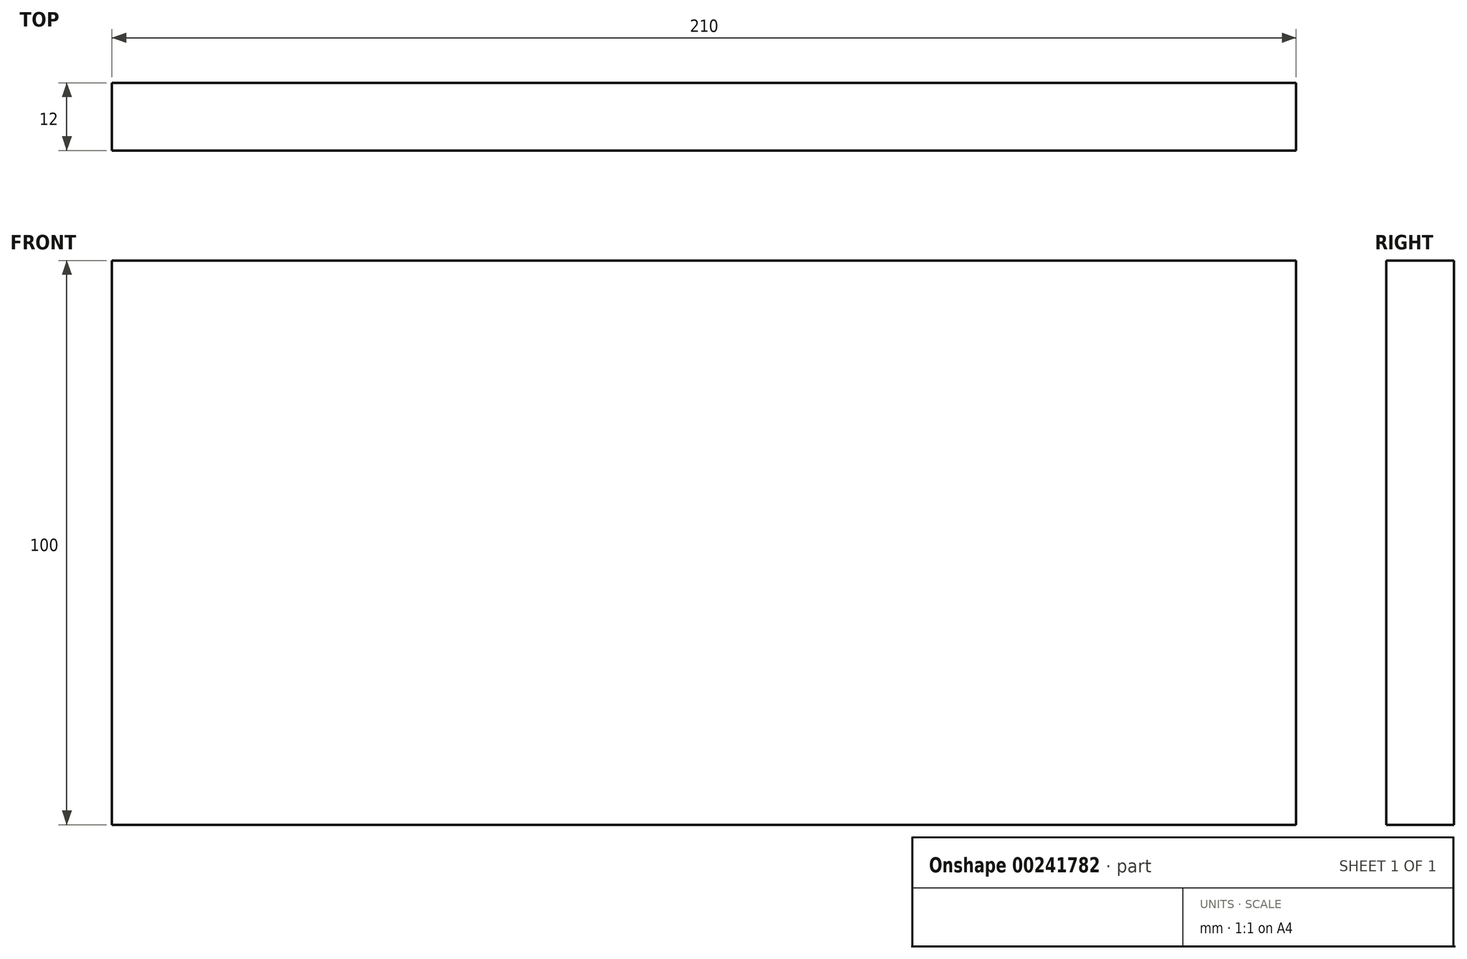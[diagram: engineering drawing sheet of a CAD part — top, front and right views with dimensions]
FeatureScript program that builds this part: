
annotation { "Feature Type Name" : "Feature", "Feature Type Description" : "" }
export const myFeature = defineFeature(function(context is Context, id is Id, definition is map)
    precondition{}
    {
        {
            var Q0;
            Q0=qCreatedBy(makeId("Front.planeOp"),FACE);
            var sketch = newSketch(context, id + "F0", { "sketchPlane" : qUnion([Q0])});
            skLineSegment(sketch, "E0.bottom", {"start": v(0, 0) * mm, "end": v(210, 0) * mm});
            skLineSegment(sketch, "E0.top", {"start": v(0, 100) * mm, "end": v(210, 100) * mm});
            skLineSegment(sketch, "E0.left", {"start": v(0, 0) * mm, "end": v(0, 100) * mm});
            skLineSegment(sketch, "E0.right", {"start": v(210, 0) * mm, "end": v(210, 100) * mm});
            skSolve(sketch);
        }
        {
            var Q0;
            Q0=qSketchRegion(id+"F0",true);
            extrude(context, id + "F1", {"entities" : qUnion([Q0]), "depth" : 12 * mm});
        }
    });
